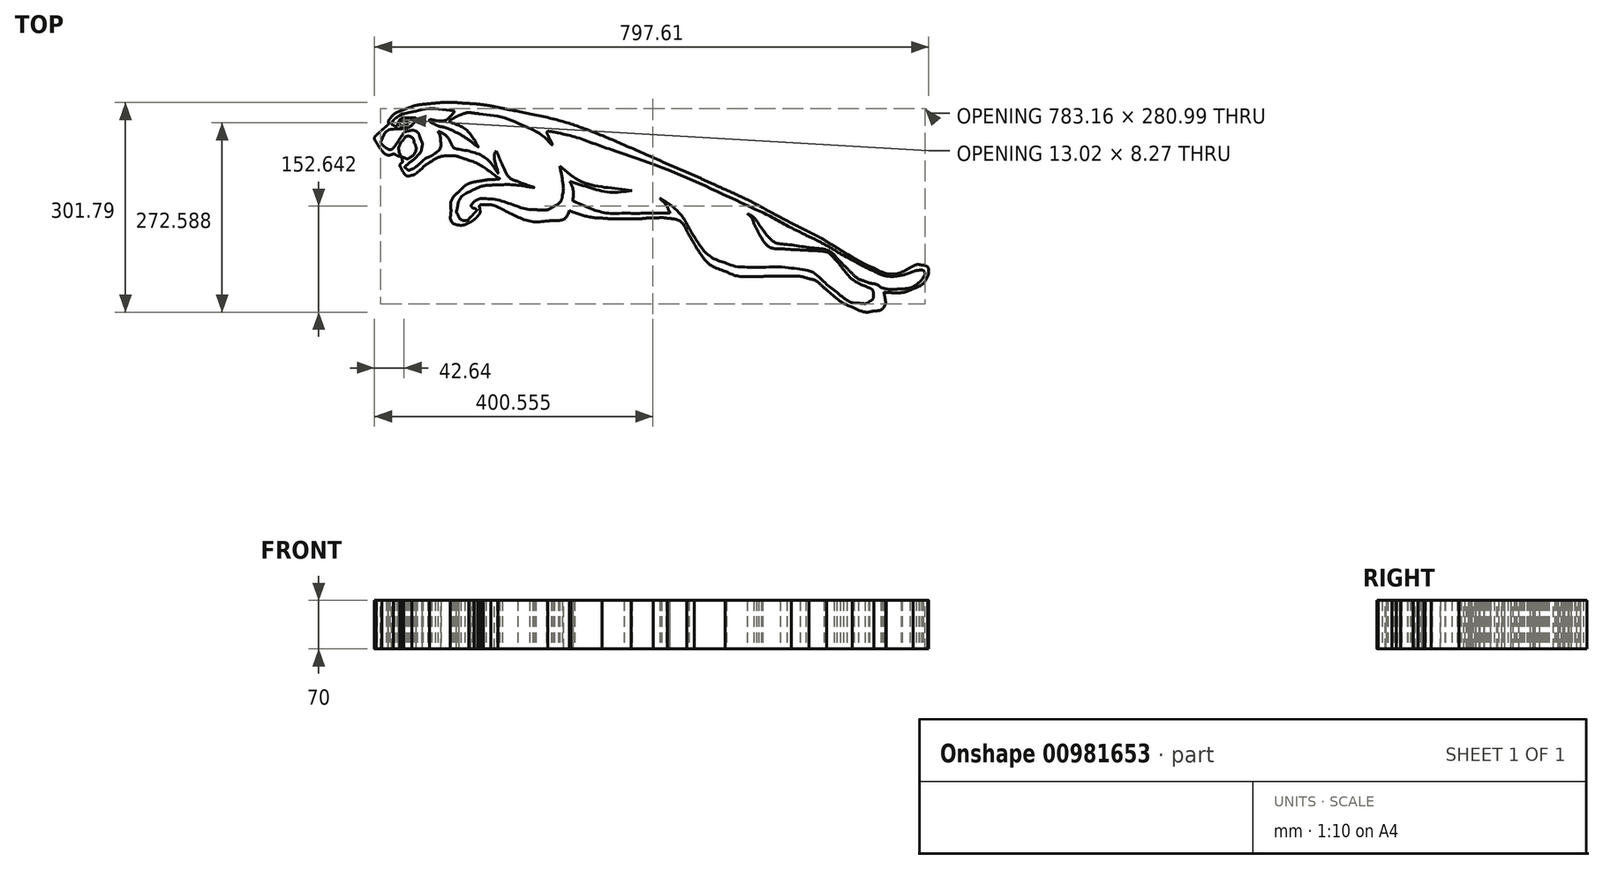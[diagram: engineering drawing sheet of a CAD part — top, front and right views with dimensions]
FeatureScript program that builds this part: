
annotation { "Feature Type Name" : "Feature", "Feature Type Description" : "" }
export const myFeature = defineFeature(function(context is Context, id is Id, definition is map)
    precondition{}
    {
        {
            var Q0;
            Q0=qCreatedBy(makeId("Top.planeOp"),FACE);
            var sketch = newSketch(context, id + "F0", { "sketchPlane" : qUnion([Q0])});
            skFitSpline(sketch, "E0", {"points": [v(-630.61, 313.95) * mm, v(-623.01, 313.31) * mm, v(-615.42, 312.58) * mm, v(-607.8, 312.06) * mm]});
            skFitSpline(sketch, "E1", {"points": [v(-607.8, 312.06) * mm, v(-564.54, 309.1) * mm, v(-521.8, 302.4) * mm, v(-479.42, 293.43) * mm]});
            skFitSpline(sketch, "E2", {"points": [v(-479.42, 293.43) * mm, v(-342.65, 264.44) * mm, v(-211.31, 218.77) * mm, v(-83.3, 163.18) * mm]});
            skFitSpline(sketch, "E3", {"points": [v(-83.3, 163.18) * mm, v(-14.33, 133.24) * mm, v(54.68, 103.37) * mm, v(123.05, 72.13) * mm]});
            skFitSpline(sketch, "E4", {"points": [v(123.05, 72.13) * mm, v(208.28, 33.18) * mm, v(290.82, -11.23) * mm, v(374.14, -54.04) * mm]});
            skFitSpline(sketch, "E5", {"points": [v(374.14, -54.04) * mm, v(421.57, -78.42) * mm, v(466.82, -106.5) * mm, v(512.74, -133.46) * mm]});
            skFitSpline(sketch, "E6", {"points": [v(512.74, -133.46) * mm, v(530.93, -144.13) * mm, v(549.79, -153.91) * mm, v(569.1, -162.39) * mm]});
            skFitSpline(sketch, "E7", {"points": [v(569.1, -162.39) * mm, v(603.9, -177.67) * mm, v(639.18, -178.12) * mm, v(673.9, -161.44) * mm]});
            skFitSpline(sketch, "E8", {"points": [v(673.9, -161.44) * mm, v(684.59, -156.3) * mm, v(695.26, -152.3) * mm, v(707.43, -154.04) * mm]});
            skFitSpline(sketch, "E9", {"points": [v(707.43, -154.04) * mm, v(718.46, -155.62) * mm, v(726.83, -162.07) * mm, v(727.59, -171.64) * mm]});
            skFitSpline(sketch, "E10", {"points": [v(727.59, -171.64) * mm, v(727.97, -176.49) * mm, v(726.73, -182.06) * mm, v(724.49, -186.41) * mm]});
            skFitSpline(sketch, "E11", {"points": [v(724.49, -186.41) * mm, v(715.53, -203.8) * mm, v(700.7, -214.79) * mm, v(682.93, -222.01) * mm]});
            skFitSpline(sketch, "E12", {"points": [v(682.93, -222.01) * mm, v(658.01, -232.15) * mm, v(631.9, -233.93) * mm, v(605.39, -232.58) * mm]});
            skFitSpline(sketch, "E13", {"points": [v(605.39, -232.58) * mm, v(603.27, -232.48) * mm, v(601.15, -232.28) * mm, v(598.96, -232.12) * mm]});
            skFitSpline(sketch, "E14", {"points": [v(598.96, -232.12) * mm, v(599.88, -237.16) * mm, v(601.07, -241.68) * mm, v(601.49, -246.27) * mm]});
            skFitSpline(sketch, "E15", {"points": [v(601.49, -246.27) * mm, v(603.35, -266.86) * mm, v(590.93, -282.73) * mm, v(570.62, -286.02) * mm]});
            skFitSpline(sketch, "E16", {"points": [v(570.62, -286.02) * mm, v(548.55, -289.6) * mm, v(527.9, -284.46) * mm, v(508.05, -275.4) * mm]});
            skFitSpline(sketch, "E17", {"points": [v(508.05, -275.4) * mm, v(480.52, -262.83) * mm, v(456.57, -244.9) * mm, v(433.9, -225.1) * mm]});
            skFitSpline(sketch, "E18", {"points": [v(433.9, -225.1) * mm, v(418.83, -211.93) * mm, v(403.61, -199.06) * mm, v(383.76, -193.24) * mm]});
            skFitSpline(sketch, "E19", {"points": [v(383.76, -193.24) * mm, v(367.16, -188.38) * mm, v(350.24, -185.59) * mm, v(333.06, -185.55) * mm]});
            skFitSpline(sketch, "E20", {"points": [v(333.06, -185.55) * mm, v(303.27, -185.5) * mm, v(273.46, -185.99) * mm, v(243.67, -186.8) * mm]});
            skFitSpline(sketch, "E21", {"points": [v(243.67, -186.8) * mm, v(208.9, -187.75) * mm, v(174.78, -184.97) * mm, v(142.17, -171.77) * mm]});
            skFitSpline(sketch, "E22", {"points": [v(142.17, -171.77) * mm, v(103.21, -156.01) * mm, v(75.08, -127.96) * mm, v(53.34, -92.86) * mm]});
            skFitSpline(sketch, "E23", {"points": [v(53.34, -92.86) * mm, v(45.71, -80.55) * mm, v(38.33, -68.06) * mm, v(31.4, -55.35) * mm]});
            skFitSpline(sketch, "E24", {"points": [v(31.4, -55.35) * mm, v(19.46, -33.42) * mm, v(0.16, -22.41) * mm, v(-23.56, -19.24) * mm]});
            skFitSpline(sketch, "E25", {"points": [v(-23.56, -19.24) * mm, v(-37, -17.45) * mm, v(-50.82, -17.88) * mm, v(-64.44, -18.27) * mm]});
            skFitSpline(sketch, "E26", {"points": [v(-64.44, -18.27) * mm, v(-85.73, -18.88) * mm, v(-107, -21.14) * mm, v(-128.29, -21.2) * mm]});
            skFitSpline(sketch, "E27", {"points": [v(-128.29, -21.2) * mm, v(-156.23, -21.27) * mm, v(-184.25, -20.92) * mm, v(-212.1, -18.86) * mm]});
            skFitSpline(sketch, "E28", {"points": [v(-212.1, -18.86) * mm, v(-243.06, -16.56) * mm, v(-273.12, -8.9) * mm, v(-302.45, 1.4) * mm]});
            skFitSpline(sketch, "E29", {"points": [v(-302.45, 1.4) * mm, v(-303.69, 1.83) * mm, v(-304.92, 2.3) * mm, v(-306.3, 2.8) * mm]});
            skFitSpline(sketch, "E30", {"points": [v(-306.3, 2.8) * mm, v(-320.32, -21.13) * mm, v(-343.94, -25.65) * mm, v(-368.29, -26.78) * mm]});
            skFitSpline(sketch, "E31", {"points": [v(-368.29, -26.78) * mm, v(-412.85, -28.83) * mm, v(-454.01, -15.8) * mm, v(-493.5, 3.77) * mm]});
            skFitSpline(sketch, "E32", {"points": [v(-493.5, 3.77) * mm, v(-512.46, 13.16) * mm, v(-532.31, 19.66) * mm, v(-553.86, 19.2) * mm]});
            skFitSpline(sketch, "E33", {"points": [v(-553.86, 19.2) * mm, v(-563.11, 19.01) * mm, v(-564.82, 16.96) * mm, v(-563.76, 7.68) * mm]});
            skFitSpline(sketch, "E34", {"points": [v(-563.76, 7.68) * mm, v(-562.94, 0.43) * mm, v(-564.55, -6.22) * mm, v(-569.2, -11.99) * mm]});
            skFitSpline(sketch, "E35", {"points": [v(-569.2, -11.99) * mm, v(-576.26, -20.7) * mm, v(-584.98, -27.6) * mm, v(-595.27, -31.64) * mm]});
            skFitSpline(sketch, "E36", {"points": [v(-595.27, -31.64) * mm, v(-615.05, -39.4) * mm, v(-644.67, -29.86) * mm, v(-646.6, 1.9) * mm]});
            skFitSpline(sketch, "E37", {"points": [v(-646.6, 1.9) * mm, v(-647.98, 24.7) * mm, v(-639.35, 43.08) * mm, v(-623.07, 58.4) * mm]});
            skFitSpline(sketch, "E38", {"points": [v(-623.07, 58.4) * mm, v(-603.35, 76.96) * mm, v(-578.99, 85.47) * mm, v(-553.01, 89.7) * mm]});
            skFitSpline(sketch, "E39", {"points": [v(-553.01, 89.7) * mm, v(-538.94, 92) * mm, v(-524.56, 92.42) * mm, v(-510.31, 93.69) * mm]});
            skFitSpline(sketch, "E40", {"points": [v(-510.31, 93.69) * mm, v(-509.4, 93.77) * mm, v(-508.48, 93.88) * mm, v(-506.71, 95.23) * mm]});
            skFitSpline(sketch, "E41", {"points": [v(-506.71, 95.23) * mm, v(-507.36, 95.43) * mm, v(-508.12, 95.48) * mm, v(-508.64, 95.86) * mm]});
            skFitSpline(sketch, "E42", {"points": [v(-508.64, 95.86) * mm, v(-539.26, 118.22) * mm, v(-571.13, 138.4) * mm, v(-606.95, 151.54) * mm]});
            skFitSpline(sketch, "E43", {"points": [v(-606.95, 151.54) * mm, v(-620.58, 156.54) * mm, v(-634.55, 160.43) * mm, v(-649.27, 160.18) * mm]});
            skFitSpline(sketch, "E44", {"points": [v(-649.27, 160.18) * mm, v(-670.86, 159.82) * mm, v(-690.52, 152.48) * mm, v(-708.53, 141.4) * mm]});
            skFitSpline(sketch, "E45", {"points": [v(-708.53, 141.4) * mm, v(-719.33, 134.76) * mm, v(-728.85, 125.93) * mm, v(-738.53, 117.6) * mm]});
            skFitSpline(sketch, "E46", {"points": [v(-738.53, 117.6) * mm, v(-744.9, 112.09) * mm, v(-751.25, 106.87) * mm, v(-759.6, 104.75) * mm]});
            skFitSpline(sketch, "E47", {"points": [v(-759.6, 104.75) * mm, v(-769.27, 102.3) * mm, v(-777.56, 104.57) * mm, v(-783.57, 112.66) * mm]});
            skFitSpline(sketch, "E48", {"points": [v(-783.57, 112.66) * mm, v(-786.4, 116.49) * mm, v(-788.45, 120.94) * mm, v(-790.55, 125.25) * mm]});
            skFitSpline(sketch, "E49", {"points": [v(-790.55, 125.25) * mm, v(-793.5, 131.3) * mm, v(-792.79, 136.76) * mm, v(-787.64, 141.58) * mm]});
            skFitSpline(sketch, "E50", {"points": [v(-787.64, 141.58) * mm, v(-786.68, 142.48) * mm, v(-786.54, 144.8) * mm, v(-786.77, 146.35) * mm]});
            skFitSpline(sketch, "E51", {"points": [v(-786.77, 146.35) * mm, v(-787.3, 150.07) * mm, v(-788.29, 153.72) * mm, v(-789.27, 158.22) * mm]});
            skFitSpline(sketch, "E52", {"points": [v(-789.27, 158.22) * mm, v(-784.78, 156.4) * mm, v(-781.3, 154.96) * mm, v(-777.79, 153.58) * mm]});
            skFitSpline(sketch, "E53", {"points": [v(-777.79, 153.58) * mm, v(-773.94, 152.07) * mm, v(-770.4, 152.52) * mm, v(-766.9, 154.88) * mm]});
            skFitSpline(sketch, "E54", {"points": [v(-766.9, 154.88) * mm, v(-753.53, 163.93) * mm, v(-747.17, 183.21) * mm, v(-752.68, 198.37) * mm]});
            skFitSpline(sketch, "E55", {"points": [v(-752.68, 198.37) * mm, v(-757.86, 212.62) * mm, v(-774.31, 216.81) * mm, v(-784.85, 205.85) * mm]});
            skFitSpline(sketch, "E56", {"points": [v(-784.85, 205.85) * mm, v(-789.78, 200.73) * mm, v(-793.7, 194.1) * mm, v(-796.28, 187.45) * mm]});
            skFitSpline(sketch, "E57", {"points": [v(-796.28, 187.45) * mm, v(-797.97, 183.09) * mm, v(-797, 177.38) * mm, v(-796.16, 172.46) * mm]});
            skFitSpline(sketch, "E58", {"points": [v(-796.16, 172.46) * mm, v(-795.45, 168.33) * mm, v(-793.19, 164.46) * mm, v(-791.44, 160.05) * mm]});
            skFitSpline(sketch, "E59", {"points": [v(-791.44, 160.05) * mm, v(-798, 159.9) * mm, v(-803.3, 161.95) * mm, v(-808.39, 164.95) * mm]});
            skFitSpline(sketch, "E60", {"points": [v(-808.39, 164.95) * mm, v(-809.63, 165.68) * mm, v(-811.44, 166.37) * mm, v(-812.7, 166.03) * mm]});
            skFitSpline(sketch, "E61", {"points": [v(-812.7, 166.03) * mm, v(-826.32, 162.38) * mm, v(-837.7, 166.75) * mm, v(-846.43, 176.85) * mm]});
            skFitSpline(sketch, "E62", {"points": [v(-846.43, 176.85) * mm, v(-852.8, 184.21) * mm, v(-858.12, 192.64) * mm, v(-862.9, 201.16) * mm]});
            skFitSpline(sketch, "E63", {"points": [v(-862.9, 201.16) * mm, v(-866.9, 208.3) * mm, v(-866, 216.02) * mm, v(-859.86, 221.84) * mm]});
            skFitSpline(sketch, "E64", {"points": [v(-859.86, 221.84) * mm, v(-850.08, 231.09) * mm, v(-839.91, 239.94) * mm, v(-829.68, 248.69) * mm]});
            skFitSpline(sketch, "E65", {"points": [v(-829.68, 248.69) * mm, v(-827.24, 250.77) * mm, v(-826.6, 252.48) * mm, v(-826.63, 255.73) * mm]});
            skFitSpline(sketch, "E66", {"points": [v(-826.63, 255.73) * mm, v(-826.65, 259.35) * mm, v(-825.52, 263.77) * mm, v(-823.26, 266.48) * mm]});
            skFitSpline(sketch, "E67", {"points": [v(-823.26, 266.48) * mm, v(-811.62, 280.44) * mm, v(-795.95, 288.55) * mm, v(-779.26, 294.82) * mm]});
            skFitSpline(sketch, "E68", {"points": [v(-779.26, 294.82) * mm, v(-753.04, 304.68) * mm, v(-725.67, 309.2) * mm, v(-697.92, 311.89) * mm]});
            skFitSpline(sketch, "E69", {"points": [v(-697.92, 311.89) * mm, v(-690.49, 312.6) * mm, v(-683.05, 313.26) * mm, v(-675.61, 313.95) * mm]});
            skFitSpline(sketch, "E70", {"points": [v(-630.61, 313.95) * mm, v(-623.01, 313.31) * mm, v(-615.42, 312.58) * mm, v(-607.8, 312.06) * mm, v(-564.54, 309.1) * mm, v(-521.8, 302.4) * mm, v(-479.42, 293.43) * mm, v(-342.65, 264.44) * mm, v(-211.31, 218.77) * mm, v(-83.3, 163.18) * mm]});
            skFitSpline(sketch, "E71", {"points": [v(-83.3, 163.18) * mm, v(-14.33, 133.24) * mm, v(54.68, 103.37) * mm, v(123.05, 72.13) * mm, v(208.28, 33.18) * mm, v(290.82, -11.23) * mm, v(374.14, -54.04) * mm]});
            skFitSpline(sketch, "E72", {"points": [v(374.14, -54.04) * mm, v(421.57, -78.42) * mm, v(466.82, -106.5) * mm, v(512.74, -133.46) * mm, v(530.93, -144.13) * mm, v(549.79, -153.91) * mm, v(569.1, -162.39) * mm]});
            skFitSpline(sketch, "E73", {"points": [v(569.1, -162.39) * mm, v(603.9, -177.67) * mm, v(639.18, -178.12) * mm, v(673.9, -161.44) * mm]});
            skFitSpline(sketch, "E74", {"points": [v(673.9, -161.44) * mm, v(684.59, -156.3) * mm, v(695.26, -152.3) * mm, v(707.43, -154.04) * mm]});
            skFitSpline(sketch, "E75", {"points": [v(707.43, -154.04) * mm, v(718.46, -155.62) * mm, v(726.83, -162.07) * mm, v(727.59, -171.64) * mm]});
            skFitSpline(sketch, "E76", {"points": [v(727.59, -171.64) * mm, v(727.97, -176.49) * mm, v(726.73, -182.06) * mm, v(724.49, -186.41) * mm]});
            skFitSpline(sketch, "E77", {"points": [v(724.49, -186.41) * mm, v(715.53, -203.8) * mm, v(700.7, -214.79) * mm, v(682.93, -222.01) * mm]});
            skFitSpline(sketch, "E78", {"points": [v(682.93, -222.01) * mm, v(658.01, -232.15) * mm, v(631.9, -233.93) * mm, v(605.39, -232.58) * mm]});
            skFitSpline(sketch, "E79", {"points": [v(605.39, -232.58) * mm, v(603.27, -232.48) * mm, v(601.15, -232.28) * mm, v(598.96, -232.12) * mm]});
            skFitSpline(sketch, "E80", {"points": [v(598.96, -232.12) * mm, v(599.88, -237.16) * mm, v(601.07, -241.68) * mm, v(601.49, -246.27) * mm]});
            skFitSpline(sketch, "E81", {"points": [v(601.49, -246.27) * mm, v(603.35, -266.86) * mm, v(590.93, -282.73) * mm, v(570.62, -286.02) * mm]});
            skFitSpline(sketch, "E82", {"points": [v(570.62, -286.02) * mm, v(548.55, -289.6) * mm, v(527.9, -284.46) * mm, v(508.05, -275.4) * mm]});
            skFitSpline(sketch, "E83", {"points": [v(508.05, -275.4) * mm, v(480.52, -262.83) * mm, v(456.57, -244.9) * mm, v(433.9, -225.1) * mm]});
            skFitSpline(sketch, "E84", {"points": [v(433.9, -225.1) * mm, v(418.83, -211.93) * mm, v(403.61, -199.06) * mm, v(383.76, -193.24) * mm]});
            skFitSpline(sketch, "E85", {"points": [v(383.76, -193.24) * mm, v(367.16, -188.38) * mm, v(350.24, -185.59) * mm, v(333.06, -185.55) * mm]});
            skFitSpline(sketch, "E86", {"points": [v(333.06, -185.55) * mm, v(303.27, -185.5) * mm, v(273.46, -185.99) * mm, v(243.67, -186.8) * mm]});
            skFitSpline(sketch, "E87", {"points": [v(243.67, -186.8) * mm, v(208.9, -187.75) * mm, v(174.78, -184.97) * mm, v(142.17, -171.77) * mm]});
            skFitSpline(sketch, "E88", {"points": [v(142.17, -171.77) * mm, v(103.21, -156.01) * mm, v(75.08, -127.96) * mm, v(53.34, -92.86) * mm]});
            skFitSpline(sketch, "E89", {"points": [v(53.34, -92.86) * mm, v(45.71, -80.55) * mm, v(38.33, -68.06) * mm, v(31.4, -55.35) * mm]});
            skFitSpline(sketch, "E90", {"points": [v(31.4, -55.35) * mm, v(19.46, -33.42) * mm, v(0.16, -22.41) * mm, v(-23.56, -19.24) * mm]});
            skFitSpline(sketch, "E91", {"points": [v(-23.56, -19.24) * mm, v(-37, -17.45) * mm, v(-50.82, -17.88) * mm, v(-64.44, -18.27) * mm]});
            skFitSpline(sketch, "E92", {"points": [v(-64.44, -18.27) * mm, v(-85.73, -18.88) * mm, v(-107, -21.14) * mm, v(-128.29, -21.2) * mm]});
            skFitSpline(sketch, "E93", {"points": [v(-128.29, -21.2) * mm, v(-156.23, -21.27) * mm, v(-184.25, -20.92) * mm, v(-212.1, -18.86) * mm]});
            skFitSpline(sketch, "E94", {"points": [v(-212.1, -18.86) * mm, v(-243.06, -16.56) * mm, v(-273.12, -8.9) * mm, v(-302.45, 1.4) * mm]});
            skFitSpline(sketch, "E95", {"points": [v(-302.45, 1.4) * mm, v(-303.69, 1.83) * mm, v(-304.92, 2.3) * mm, v(-306.3, 2.8) * mm]});
            skFitSpline(sketch, "E96", {"points": [v(-306.3, 2.8) * mm, v(-320.32, -21.13) * mm, v(-343.94, -25.65) * mm, v(-368.29, -26.78) * mm]});
            skFitSpline(sketch, "E97", {"points": [v(-368.29, -26.78) * mm, v(-412.85, -28.83) * mm, v(-454.01, -15.8) * mm, v(-493.5, 3.77) * mm]});
            skFitSpline(sketch, "E98", {"points": [v(-493.5, 3.77) * mm, v(-512.46, 13.16) * mm, v(-532.31, 19.66) * mm, v(-553.86, 19.2) * mm, v(-563.11, 19.01) * mm, v(-564.82, 16.96) * mm, v(-563.76, 7.68) * mm]});
            skFitSpline(sketch, "E99", {"points": [v(-563.76, 7.68) * mm, v(-562.94, 0.43) * mm, v(-564.55, -6.22) * mm, v(-569.2, -11.99) * mm]});
            skFitSpline(sketch, "E100", {"points": [v(-569.2, -11.99) * mm, v(-572.73, -16.35) * mm, v(-576.67, -20.25) * mm, v(-581.02, -23.57) * mm]});
            skFitSpline(sketch, "E101", {"points": [v(-581.02, -23.57) * mm, v(-585.37, -26.89) * mm, v(-590.12, -29.62) * mm, v(-595.27, -31.64) * mm]});
            skFitSpline(sketch, "E102", {"points": [v(-595.27, -31.64) * mm, v(-615.05, -39.4) * mm, v(-644.67, -29.86) * mm, v(-646.6, 1.9) * mm]});
            skFitSpline(sketch, "E103", {"points": [v(-646.6, 1.9) * mm, v(-647.98, 24.7) * mm, v(-639.35, 43.08) * mm, v(-623.07, 58.4) * mm]});
            skFitSpline(sketch, "E104", {"points": [v(-623.07, 58.4) * mm, v(-603.35, 76.96) * mm, v(-578.99, 85.47) * mm, v(-553.01, 89.7) * mm, v(-538.94, 92) * mm, v(-524.56, 92.42) * mm, v(-510.31, 93.69) * mm]});
            skFitSpline(sketch, "E105", {"points": [v(-510.31, 93.69) * mm, v(-509.4, 93.77) * mm, v(-508.48, 93.88) * mm, v(-506.71, 95.23) * mm]});
            skFitSpline(sketch, "E106", {"points": [v(-506.71, 95.23) * mm, v(-507.36, 95.43) * mm, v(-508.12, 95.48) * mm, v(-508.64, 95.86) * mm]});
            skFitSpline(sketch, "E107", {"points": [v(-508.64, 95.86) * mm, v(-539.26, 118.22) * mm, v(-571.13, 138.4) * mm, v(-606.95, 151.54) * mm]});
            skFitSpline(sketch, "E108", {"points": [v(-606.95, 151.54) * mm, v(-620.58, 156.54) * mm, v(-634.55, 160.43) * mm, v(-649.27, 160.18) * mm]});
            skFitSpline(sketch, "E109", {"points": [v(-649.27, 160.18) * mm, v(-670.86, 159.82) * mm, v(-690.52, 152.48) * mm, v(-708.53, 141.4) * mm]});
            skFitSpline(sketch, "E110", {"points": [v(-708.53, 141.4) * mm, v(-719.33, 134.76) * mm, v(-728.85, 125.93) * mm, v(-738.53, 117.6) * mm]});
            skFitSpline(sketch, "E111", {"points": [v(-738.53, 117.6) * mm, v(-744.9, 112.09) * mm, v(-751.25, 106.87) * mm, v(-759.6, 104.75) * mm]});
            skFitSpline(sketch, "E112", {"points": [v(-759.6, 104.75) * mm, v(-769.27, 102.3) * mm, v(-777.56, 104.57) * mm, v(-783.57, 112.66) * mm]});
            skFitSpline(sketch, "E113", {"points": [v(-783.57, 112.66) * mm, v(-786.4, 116.49) * mm, v(-788.45, 120.94) * mm, v(-790.55, 125.25) * mm]});
            skFitSpline(sketch, "E114", {"points": [v(-790.55, 125.25) * mm, v(-793.5, 131.3) * mm, v(-792.79, 136.76) * mm, v(-787.64, 141.58) * mm]});
            skFitSpline(sketch, "E115", {"points": [v(-787.64, 141.58) * mm, v(-786.68, 142.48) * mm, v(-786.54, 144.8) * mm, v(-786.77, 146.35) * mm]});
            skFitSpline(sketch, "E116", {"points": [v(-786.77, 146.35) * mm, v(-787.3, 150.07) * mm, v(-788.29, 153.72) * mm, v(-789.27, 158.22) * mm]});
            skFitSpline(sketch, "E117", {"points": [v(-789.27, 158.22) * mm, v(-784.78, 156.4) * mm, v(-781.3, 154.96) * mm, v(-777.79, 153.58) * mm]});
            skFitSpline(sketch, "E118", {"points": [v(-777.79, 153.58) * mm, v(-773.94, 152.07) * mm, v(-770.4, 152.52) * mm, v(-766.9, 154.88) * mm]});
            skFitSpline(sketch, "E119", {"points": [v(-766.9, 154.88) * mm, v(-753.53, 163.93) * mm, v(-747.17, 183.21) * mm, v(-752.68, 198.37) * mm]});
            skFitSpline(sketch, "E120", {"points": [v(-752.68, 198.37) * mm, v(-757.86, 212.62) * mm, v(-774.31, 216.81) * mm, v(-784.85, 205.85) * mm]});
            skFitSpline(sketch, "E121", {"points": [v(-784.85, 205.85) * mm, v(-789.78, 200.73) * mm, v(-793.7, 194.1) * mm, v(-796.28, 187.45) * mm]});
            skFitSpline(sketch, "E122", {"points": [v(-796.28, 187.45) * mm, v(-797.97, 183.09) * mm, v(-797, 177.38) * mm, v(-796.16, 172.46) * mm]});
            skFitSpline(sketch, "E123", {"points": [v(-796.16, 172.46) * mm, v(-795.45, 168.33) * mm, v(-793.19, 164.46) * mm, v(-791.44, 160.05) * mm]});
            skFitSpline(sketch, "E124", {"points": [v(-791.44, 160.05) * mm, v(-798, 159.9) * mm, v(-803.3, 161.95) * mm, v(-808.39, 164.95) * mm]});
            skFitSpline(sketch, "E125", {"points": [v(-808.39, 164.95) * mm, v(-809.63, 165.68) * mm, v(-811.44, 166.37) * mm, v(-812.7, 166.03) * mm]});
            skFitSpline(sketch, "E126", {"points": [v(-812.7, 166.03) * mm, v(-826.32, 162.38) * mm, v(-837.7, 166.75) * mm, v(-846.43, 176.85) * mm]});
            skFitSpline(sketch, "E127", {"points": [v(-846.43, 176.85) * mm, v(-852.8, 184.21) * mm, v(-858.12, 192.64) * mm, v(-862.9, 201.16) * mm]});
            skFitSpline(sketch, "E128", {"points": [v(-862.9, 201.16) * mm, v(-866.9, 208.3) * mm, v(-866, 216.02) * mm, v(-859.86, 221.84) * mm]});
            skFitSpline(sketch, "E129", {"points": [v(-859.86, 221.84) * mm, v(-850.08, 231.09) * mm, v(-839.91, 239.94) * mm, v(-829.68, 248.69) * mm, v(-827.24, 250.77) * mm, v(-826.6, 252.48) * mm, v(-826.63, 255.73) * mm]});
            skFitSpline(sketch, "E130", {"points": [v(-826.63, 255.73) * mm, v(-826.65, 259.35) * mm, v(-825.52, 263.77) * mm, v(-823.27, 266.48) * mm]});
            skFitSpline(sketch, "E131", {"points": [v(-823.27, 266.48) * mm, v(-811.62, 280.44) * mm, v(-795.95, 288.55) * mm, v(-779.27, 294.82) * mm, v(-753.04, 304.68) * mm, v(-725.67, 309.2) * mm, v(-697.92, 311.89) * mm, v(-690.49, 312.6) * mm, v(-683.05, 313.26) * mm, v(-675.61, 313.95) * mm]});
            skFitSpline(sketch, "E132", {"points": [v(-675.61, 313.95) * mm, v(-660.61, 313.95) * mm, v(-645.61, 313.95) * mm, v(-630.61, 313.95) * mm]});
            skFitSpline(sketch, "E133", {"points": [v(205.03, -5.67) * mm, v(219.16, -13.12) * mm, v(230.59, -23.28) * mm, v(239.13, -36.66) * mm]});
            skFitSpline(sketch, "E134", {"points": [v(239.13, -36.66) * mm, v(242.53, -41.98) * mm, v(246.44, -47) * mm, v(250.27, -52.02) * mm]});
            skFitSpline(sketch, "E135", {"points": [v(250.27, -52.02) * mm, v(267.87, -75.08) * mm, v(290.2, -90.44) * mm, v(319.5, -94.4) * mm]});
            skFitSpline(sketch, "E136", {"points": [v(319.5, -94.4) * mm, v(348.36, -98.3) * mm, v(377.19, -102.57) * mm, v(406.1, -106.03) * mm, v(428.63, -108.74) * mm, v(448.05, -116.97) * mm, v(463.7, -133.78) * mm]});
            skFitSpline(sketch, "E137", {"points": [v(463.7, -133.78) * mm, v(474.02, -144.87) * mm, v(484.74, -155.6) * mm, v(495.44, -166.35) * mm]});
            skFitSpline(sketch, "E138", {"points": [v(495.44, -166.35) * mm, v(509.75, -180.72) * mm, v(525.18, -193.38) * mm, v(544.57, -200.7) * mm]});
            skFitSpline(sketch, "E139", {"points": [v(544.57, -200.7) * mm, v(559.75, -206.41) * mm, v(576.2, -208.93) * mm, v(589.95, -218.37) * mm]});
            skFitSpline(sketch, "E140", {"points": [v(589.95, -218.37) * mm, v(591.38, -219.35) * mm, v(593.4, -219.55) * mm, v(595.19, -219.93) * mm]});
            skFitSpline(sketch, "E141", {"points": [v(595.19, -219.93) * mm, v(612.77, -223.66) * mm, v(630.55, -223.92) * mm, v(648.4, -222.68) * mm]});
            skFitSpline(sketch, "E142", {"points": [v(648.4, -222.68) * mm, v(668, -221.32) * mm, v(686.02, -215.35) * mm, v(701.25, -202.76) * mm]});
            skFitSpline(sketch, "E143", {"points": [v(701.25, -202.76) * mm, v(705.96, -198.87) * mm, v(710.23, -193.6) * mm, v(712.73, -188.08) * mm]});
            skFitSpline(sketch, "E144", {"points": [v(712.73, -188.08) * mm, v(717.26, -178.07) * mm, v(710.3, -168.73) * mm, v(699.32, -168.84) * mm]});
            skFitSpline(sketch, "E145", {"points": [v(699.32, -168.84) * mm, v(696.84, -168.86) * mm, v(694.24, -168.99) * mm, v(691.93, -169.77) * mm]});
            skFitSpline(sketch, "E146", {"points": [v(691.93, -169.77) * mm, v(683.27, -172.68) * mm, v(674.75, -176) * mm, v(666.1, -178.92) * mm]});
            skFitSpline(sketch, "E147", {"points": [v(666.1, -178.92) * mm, v(661.24, -180.56) * mm, v(656.3, -182.31) * mm, v(651.26, -182.98) * mm]});
            skFitSpline(sketch, "E148", {"points": [v(651.26, -182.98) * mm, v(623, -186.7) * mm, v(595.41, -182.77) * mm, v(569.72, -171.12) * mm]});
            skFitSpline(sketch, "E149", {"points": [v(569.72, -171.12) * mm, v(543.25, -159.1) * mm, v(517.63, -145.14) * mm, v(492.05, -131.25) * mm]});
            skFitSpline(sketch, "E150", {"points": [v(492.05, -131.25) * mm, v(469.83, -119.2) * mm, v(448.48, -105.52) * mm, v(426.21, -93.53) * mm]});
            skFitSpline(sketch, "E151", {"points": [v(426.21, -93.53) * mm, v(403.96, -81.55) * mm, v(381, -70.88) * mm, v(358.44, -59.44) * mm]});
            skFitSpline(sketch, "E152", {"points": [v(358.44, -59.44) * mm, v(313.78, -36.77) * mm, v(269.82, -12.63) * mm, v(224.46, 8.53) * mm]});
            skFitSpline(sketch, "E153", {"points": [v(224.46, 8.53) * mm, v(90.23, 71.14) * mm, v(-45.9, 129.3) * mm, v(-185.76, 178.4) * mm]});
            skFitSpline(sketch, "E154", {"points": [v(-185.76, 178.4) * mm, v(-236, 196.03) * mm, v(-286.2, 213.74) * mm, v(-337.98, 226.42) * mm]});
            skFitSpline(sketch, "E155", {"points": [v(-337.98, 226.42) * mm, v(-347, 228.63) * mm, v(-356.24, 230.07) * mm, v(-365.44, 231.44) * mm, v(-367.4, 231.74) * mm, v(-369.63, 230.22) * mm, v(-371.73, 229.54) * mm]});
            skFitSpline(sketch, "E156", {"points": [v(-371.73, 229.54) * mm, v(-371.1, 227.76) * mm, v(-370.6, 225.9) * mm, v(-369.8, 224.2) * mm]});
            skFitSpline(sketch, "E157", {"points": [v(-369.8, 224.2) * mm, v(-364.86, 213.77) * mm, v(-359.86, 203.36) * mm, v(-354.88, 192.94) * mm]});
            skFitSpline(sketch, "E158", {"points": [v(-354.88, 192.94) * mm, v(-355.38, 192.66) * mm, v(-355.88, 192.37) * mm, v(-356.38, 192.09) * mm]});
            skFitSpline(sketch, "E159", {"points": [v(-356.38, 192.09) * mm, v(-356.98, 192.55) * mm, v(-357.65, 192.95) * mm, v(-358.18, 193.48) * mm]});
            skFitSpline(sketch, "E160", {"points": [v(-358.18, 193.48) * mm, v(-381.84, 217.37) * mm, v(-409.85, 234.75) * mm, v(-440.4, 248.3) * mm, v(-480.6, 266.13) * mm, v(-522.8, 276.49) * mm, v(-566.3, 281.85) * mm]});
            skFitSpline(sketch, "E161", {"points": [v(-566.3, 281.85) * mm, v(-583.8, 284.01) * mm, v(-601.4, 284.77) * mm, v(-618.23, 278.84) * mm]});
            skFitSpline(sketch, "E162", {"points": [v(-618.23, 278.84) * mm, v(-628.32, 275.28) * mm, v(-637.75, 269.81) * mm, v(-647.31, 264.89) * mm]});
            skFitSpline(sketch, "E163", {"points": [v(-647.31, 264.89) * mm, v(-648.9, 264.07) * mm, v(-650.41, 261.65) * mm, v(-650.48, 259.9) * mm, v(-650.52, 258.8) * mm, v(-647.94, 257.4) * mm, v(-646.34, 256.47) * mm]});
            skFitSpline(sketch, "E164", {"points": [v(-646.34, 256.47) * mm, v(-644.78, 255.57) * mm, v(-642.94, 255.15) * mm, v(-641.26, 254.42) * mm]});
            skFitSpline(sketch, "E165", {"points": [v(-641.26, 254.42) * mm, v(-609.02, 240.28) * mm, v(-586.24, 215.93) * mm, v(-568.06, 186.6) * mm]});
            skFitSpline(sketch, "E166", {"points": [v(-568.06, 186.6) * mm, v(-567.98, 186.48) * mm, v(-568.27, 186.12) * mm, v(-568.48, 185.7) * mm]});
            skFitSpline(sketch, "E167", {"points": [v(-568.48, 185.7) * mm, v(-570.35, 187.13) * mm, v(-572.2, 188.53) * mm, v(-574.04, 189.95) * mm]});
            skFitSpline(sketch, "E168", {"points": [v(-574.04, 189.95) * mm, v(-592.36, 204.16) * mm, v(-611.47, 217.2) * mm, v(-632.05, 227.94) * mm]});
            skFitSpline(sketch, "E169", {"points": [v(-632.05, 227.94) * mm, v(-645.8, 235.12) * mm, v(-660.01, 240.87) * mm, v(-675.27, 244.44) * mm]});
            skFitSpline(sketch, "E170", {"points": [v(-675.27, 244.44) * mm, v(-684.48, 246.6) * mm, v(-693.22, 251.16) * mm, v(-701.81, 255.38) * mm]});
            skFitSpline(sketch, "E171", {"points": [v(-701.81, 255.38) * mm, v(-705.38, 257.14) * mm, v(-708.53, 260.53) * mm, v(-708.42, 265.67) * mm]});
            skFitSpline(sketch, "E172", {"points": [v(-708.42, 265.67) * mm, v(-705.72, 265.18) * mm, v(-703.46, 264.7) * mm, v(-701.17, 264.36) * mm, v(-677.4, 260.88) * mm, v(-656.61, 266.8) * mm, v(-639.55, 284.15) * mm, v(-638.31, 285.4) * mm, v(-637.93, 287.5) * mm, v(-637.14, 289.22) * mm]});
            skFitSpline(sketch, "E173", {"points": [v(-637.14, 289.22) * mm, v(-638.75, 289.88) * mm, v(-640.32, 290.96) * mm, v(-641.98, 291.14) * mm, v(-679.25, 295.26) * mm, v(-716.43, 295.75) * mm, v(-753.35, 287.94) * mm, v(-770.64, 284.29) * mm, v(-787.93, 280.43) * mm, v(-803.14, 270.88) * mm]});
            skFitSpline(sketch, "E174", {"points": [v(-803.14, 270.88) * mm, v(-807.55, 268.1) * mm, v(-811.47, 264.25) * mm, v(-814.85, 260.24) * mm]});
            skFitSpline(sketch, "E175", {"points": [v(-814.85, 260.24) * mm, v(-818.24, 256.23) * mm, v(-816.63, 250.74) * mm, v(-812.2, 248.3) * mm, v(-806.91, 245.4) * mm, v(-802.58, 246.64) * mm, v(-800.28, 251.7) * mm]});
            skFitSpline(sketch, "E176", {"points": [v(-800.28, 251.7) * mm, v(-795.12, 263) * mm, v(-786.66, 269.5) * mm, v(-773.94, 269.87) * mm, v(-771.28, 269.95) * mm, v(-768.62, 270.34) * mm, v(-765.96, 270.24) * mm, v(-759.1, 270) * mm, v(-752.1, 270.34) * mm, v(-745.32, 266.64) * mm]});
            skFitSpline(sketch, "E177", {"points": [v(-745.32, 266.64) * mm, v(-756.62, 252.41) * mm, v(-769.7, 241.9) * mm, v(-787.84, 239.36) * mm]});
            skFitSpline(sketch, "E178", {"points": [v(-787.84, 239.36) * mm, v(-793.27, 238.6) * mm, v(-798.82, 238.7) * mm, v(-804.27, 238.05) * mm, v(-823.25, 235.8) * mm, v(-837.04, 225.9) * mm, v(-845.8, 209.04) * mm, v(-848.62, 203.64) * mm, v(-848.93, 197.8) * mm, v(-844.76, 193.08) * mm]});
            skFitSpline(sketch, "E179", {"points": [v(-844.76, 193.08) * mm, v(-841.3, 189.17) * mm, v(-837.2, 185.45) * mm, v(-832.66, 182.96) * mm]});
            skFitSpline(sketch, "E180", {"points": [v(-832.66, 182.96) * mm, v(-824.16, 178.31) * mm, v(-816.17, 180.13) * mm, v(-809.67, 187.35) * mm]});
            skFitSpline(sketch, "E181", {"points": [v(-809.67, 187.35) * mm, v(-807.23, 190.05) * mm, v(-805.2, 193.14) * mm, v(-803.19, 196.19) * mm]});
            skFitSpline(sketch, "E182", {"points": [v(-803.19, 196.19) * mm, v(-797.58, 204.65) * mm, v(-792.25, 213.3) * mm, v(-786.49, 221.65) * mm]});
            skFitSpline(sketch, "E183", {"points": [v(-786.49, 221.65) * mm, v(-782.53, 227.39) * mm, v(-776.73, 230.72) * mm, v(-769.84, 231.73) * mm]});
            skFitSpline(sketch, "E184", {"points": [v(-769.84, 231.73) * mm, v(-755.23, 233.88) * mm, v(-741.37, 226.63) * mm, v(-735.67, 212.97) * mm, v(-730.7, 201.06) * mm, v(-729.4, 191.4) * mm, v(-731.13, 182.91) * mm]});
            skFitSpline(sketch, "E185", {"points": [v(-731.13, 182.91) * mm, v(-732.87, 174.42) * mm, v(-737.63, 167.08) * mm, v(-744.8, 159.78) * mm]});
            skFitSpline(sketch, "E186", {"points": [v(-744.8, 159.78) * mm, v(-754.1, 150.32) * mm, v(-764.66, 142.09) * mm, v(-774.9, 133.58) * mm]});
            skFitSpline(sketch, "E187", {"points": [v(-774.9, 133.58) * mm, v(-779.63, 129.63) * mm, v(-780, 127.33) * mm, v(-775.28, 123.38) * mm]});
            skFitSpline(sketch, "E188", {"points": [v(-775.28, 123.38) * mm, v(-771.88, 120.55) * mm, v(-767.91, 118.89) * mm, v(-763.7, 120.53) * mm]});
            skFitSpline(sketch, "E189", {"points": [v(-763.7, 120.53) * mm, v(-758.82, 122.44) * mm, v(-753.74, 124.51) * mm, v(-749.64, 127.67) * mm]});
            skFitSpline(sketch, "E190", {"points": [v(-749.64, 127.67) * mm, v(-742.14, 133.46) * mm, v(-735.2, 139.97) * mm, v(-728.24, 146.42) * mm]});
            skFitSpline(sketch, "E191", {"points": [v(-728.24, 146.42) * mm, v(-724.07, 150.3) * mm, v(-719.7, 153.34) * mm, v(-714.34, 155.66) * mm]});
            skFitSpline(sketch, "E192", {"points": [v(-714.34, 155.66) * mm, v(-706.62, 158.99) * mm, v(-699.04, 163.16) * mm, v(-692.37, 168.25) * mm]});
            skFitSpline(sketch, "E193", {"points": [v(-692.37, 168.25) * mm, v(-681.1, 176.86) * mm, v(-675.81, 188.76) * mm, v(-676.62, 203.18) * mm, v(-677.19, 213.22) * mm, v(-679.77, 222.65) * mm, v(-684.69, 231.76) * mm]});
            skFitSpline(sketch, "E194", {"points": [v(-684.69, 231.76) * mm, v(-680.15, 230.19) * mm, v(-675.78, 228.57) * mm, v(-671.96, 226.1) * mm, v(-660.61, 218.72) * mm, v(-652.87, 208.1) * mm, v(-646.79, 196.27) * mm]});
            skFitSpline(sketch, "E195", {"points": [v(-646.79, 196.27) * mm, v(-642.15, 187.24) * mm, v(-635.43, 181.77) * mm, v(-625.2, 179.62) * mm]});
            skFitSpline(sketch, "E196", {"points": [v(-625.2, 179.62) * mm, v(-579.72, 170.03) * mm, v(-540.91, 149.17) * mm, v(-512.51, 111.27) * mm]});
            skFitSpline(sketch, "E197", {"points": [v(-512.51, 111.27) * mm, v(-512.12, 110.75) * mm, v(-511.54, 110.36) * mm, v(-510.55, 109.45) * mm]});
            skFitSpline(sketch, "E198", {"points": [v(-510.55, 109.45) * mm, v(-520.18, 143.25) * mm, v(-522.03, 165.88) * mm, v(-516.32, 174.5) * mm]});
            skFitSpline(sketch, "E199", {"points": [v(-516.32, 174.5) * mm, v(-510.62, 161.3) * mm, v(-505, 147.8) * mm, v(-498.98, 134.48) * mm]});
            skFitSpline(sketch, "E200", {"points": [v(-498.98, 134.48) * mm, v(-489.62, 113.74) * mm, v(-476.6, 96.14) * mm, v(-454.93, 86.86) * mm]});
            skFitSpline(sketch, "E201", {"points": [v(-454.93, 86.86) * mm, v(-443.8, 82.1) * mm, v(-432.33, 78.07) * mm, v(-420.94, 73.91) * mm]});
            skFitSpline(sketch, "E202", {"points": [v(-420.94, 73.91) * mm, v(-416.29, 72.21) * mm, v(-411.44, 71.05) * mm, v(-406.69, 69.64) * mm]});
            skFitSpline(sketch, "E203", {"points": [v(-406.69, 69.64) * mm, v(-408.36, 69) * mm, v(-409.84, 69.08) * mm, v(-411.3, 69.32) * mm]});
            skFitSpline(sketch, "E204", {"points": [v(-411.3, 69.32) * mm, v(-445.56, 74.95) * mm, v(-480.02, 77.77) * mm, v(-514.77, 76.62) * mm]});
            skFitSpline(sketch, "E205", {"points": [v(-514.77, 76.62) * mm, v(-539.3, 75.8) * mm, v(-563.1, 71.8) * mm, v(-585.44, 61.1) * mm]});
            skFitSpline(sketch, "E206", {"points": [v(-585.44, 61.1) * mm, v(-606.2, 51.15) * mm, v(-621.63, 36.42) * mm, v(-628.07, 13.61) * mm, v(-630.26, 5.84) * mm, v(-630.67, -1.78) * mm, v(-626.76, -9.2) * mm]});
            skFitSpline(sketch, "E207", {"points": [v(-626.76, -9.2) * mm, v(-620.04, -21.97) * mm, v(-603.33, -26.04) * mm, v(-592.29, -17) * mm]});
            skFitSpline(sketch, "E208", {"points": [v(-592.29, -17) * mm, v(-586.93, -12.62) * mm, v(-582.43, -7.16) * mm, v(-577.78, -1.97) * mm]});
            skFitSpline(sketch, "E209", {"points": [v(-577.78, -1.97) * mm, v(-573.4, 2.92) * mm, v(-574.36, 7.02) * mm, v(-580.62, 9.53) * mm]});
            skFitSpline(sketch, "E210", {"points": [v(-580.62, 9.53) * mm, v(-586.65, 11.94) * mm, v(-588.8, 18.4) * mm, v(-584.94, 23.57) * mm]});
            skFitSpline(sketch, "E211", {"points": [v(-584.94, 23.57) * mm, v(-582.12, 27.36) * mm, v(-577.84, 30.6) * mm, v(-573.53, 32.65) * mm]});
            skFitSpline(sketch, "E212", {"points": [v(-573.53, 32.65) * mm, v(-565.13, 36.6) * mm, v(-555.94, 37.5) * mm, v(-546.67, 36.96) * mm]});
            skFitSpline(sketch, "E213", {"points": [v(-546.67, 36.96) * mm, v(-519.99, 35.41) * mm, v(-494.46, 28.56) * mm, v(-469.4, 19.81) * mm, v(-447.77, 12.25) * mm, v(-425.73, 6.7) * mm, v(-402.78, 5.48) * mm]});
            skFitSpline(sketch, "E214", {"points": [v(-402.78, 5.48) * mm, v(-384.25, 4.5) * mm, v(-366.14, 6.38) * mm, v(-349.62, 15.86) * mm]});
            skFitSpline(sketch, "E215", {"points": [v(-349.62, 15.86) * mm, v(-337.15, 23.03) * mm, v(-328.89, 33.33) * mm, v(-326.14, 47.76) * mm]});
            skFitSpline(sketch, "E216", {"points": [v(-326.14, 47.76) * mm, v(-323.43, 62.03) * mm, v(-324.04, 76.32) * mm, v(-326.2, 90.51) * mm, v(-328.31, 104.45) * mm, v(-331.23, 118.27) * mm, v(-333.75, 131.9) * mm]});
            skFitSpline(sketch, "E217", {"points": [v(-333.75, 131.9) * mm, v(-272.36, 86.56) * mm, v(-200.85, 69.54) * mm, v(-126.4, 60.84) * mm]});
            skFitSpline(sketch, "E218", {"points": [v(-126.4, 60.84) * mm, v(-187.48, 55.68) * mm, v(-246.06, 68.65) * mm, v(-304.63, 86.6) * mm]});
            skFitSpline(sketch, "E219", {"points": [v(-304.63, 86.6) * mm, v(-297.01, 69.45) * mm, v(-294.72, 52.24) * mm, v(-295.79, 34.56) * mm]});
            skFitSpline(sketch, "E220", {"points": [v(-295.79, 34.56) * mm, v(-296.02, 30.78) * mm, v(-293.77, 30.14) * mm, v(-291.36, 29.07) * mm]});
            skFitSpline(sketch, "E221", {"points": [v(-291.36, 29.07) * mm, v(-246, 8.98) * mm, v(-198.83, -3.97) * mm, v(-148.99, -4.55) * mm]});
            skFitSpline(sketch, "E222", {"points": [v(-148.99, -4.55) * mm, v(-106.52, -5.04) * mm, v(-64.04, -4.2) * mm, v(-21.57, -4.03) * mm]});
            skFitSpline(sketch, "E223", {"points": [v(-21.57, -4.03) * mm, v(-18.12, -4.01) * mm, v(-17.17, -2.25) * mm, v(-18.37, 0.3) * mm]});
            skFitSpline(sketch, "E224", {"points": [v(-18.37, 0.3) * mm, v(-21.3, 6.56) * mm, v(-24, 13.1) * mm, v(-28.04, 18.62) * mm]});
            skFitSpline(sketch, "E225", {"points": [v(-28.04, 18.62) * mm, v(-32.98, 25.38) * mm, v(-39.2, 31.2) * mm, v(-45.49, 38.13) * mm]});
            skFitSpline(sketch, "E226", {"points": [v(-45.49, 38.13) * mm, v(-43.6, 37.24) * mm, v(-42.38, 36.8) * mm, v(-41.31, 36.14) * mm]});
            skFitSpline(sketch, "E227", {"points": [v(-41.31, 36.14) * mm, v(-35.82, 32.68) * mm, v(-30.05, 29.58) * mm, v(-24.95, 25.61) * mm]});
            skFitSpline(sketch, "E228", {"points": [v(-24.95, 25.61) * mm, v(0.84, 5.52) * mm, v(21.88, -18.74) * mm, v(38.12, -47.16) * mm]});
            skFitSpline(sketch, "E229", {"points": [v(38.12, -47.16) * mm, v(43.32, -56.26) * mm, v(48.52, -65.4) * mm, v(54.38, -74.08) * mm]});
            skFitSpline(sketch, "E230", {"points": [v(54.38, -74.08) * mm, v(77.34, -108.06) * mm, v(106.86, -134.1) * mm, v(145.8, -148.51) * mm]});
            skFitSpline(sketch, "E231", {"points": [v(145.8, -148.51) * mm, v(166.98, -156.35) * mm, v(188.93, -159.6) * mm, v(211.39, -159.98) * mm, v(251.84, -160.68) * mm, v(292.34, -158.65) * mm, v(332.73, -162.97) * mm]});
            skFitSpline(sketch, "E232", {"points": [v(332.73, -162.97) * mm, v(366.84, -166.61) * mm, v(397.92, -176.73) * mm, v(424.13, -199.97) * mm, v(440.32, -214.34) * mm, v(457.18, -227.98) * mm, v(474.22, -241.33) * mm]});
            skFitSpline(sketch, "E233", {"points": [v(474.22, -241.33) * mm, v(489.19, -253.05) * mm, v(505.67, -261.97) * mm, v(525.17, -263.7) * mm]});
            skFitSpline(sketch, "E234", {"points": [v(525.17, -263.7) * mm, v(536.6, -264.7) * mm, v(547.88, -264.86) * mm, v(558.03, -258.34) * mm]});
            skFitSpline(sketch, "E235", {"points": [v(558.03, -258.34) * mm, v(565.96, -253.24) * mm, v(569.22, -245.62) * mm, v(568.29, -236.5) * mm]});
            skFitSpline(sketch, "E236", {"points": [v(568.29, -236.5) * mm, v(567.4, -227.84) * mm, v(562.35, -222.18) * mm, v(554.27, -218.66) * mm]});
            skFitSpline(sketch, "E237", {"points": [v(554.27, -218.66) * mm, v(526.57, -206.58) * mm, v(502.2, -189.88) * mm, v(482.77, -166.4) * mm]});
            skFitSpline(sketch, "E238", {"points": [v(482.77, -166.4) * mm, v(474.08, -155.88) * mm, v(465.81, -144.85) * mm, v(456.04, -135.41) * mm]});
            skFitSpline(sketch, "E239", {"points": [v(456.04, -135.41) * mm, v(438.01, -118) * mm, v(414.91, -113.33) * mm, v(390.75, -112.08) * mm]});
            skFitSpline(sketch, "E240", {"points": [v(390.75, -112.08) * mm, v(360.83, -110.54) * mm, v(330.9, -109.06) * mm, v(301.01, -106.89) * mm]});
            skFitSpline(sketch, "E241", {"points": [v(301.01, -106.89) * mm, v(277.24, -105.16) * mm, v(258.63, -93.66) * mm, v(245.65, -73.77) * mm]});
            skFitSpline(sketch, "E242", {"points": [v(245.65, -73.77) * mm, v(240.5, -65.87) * mm, v(236.53, -57.16) * mm, v(232.35, -48.67) * mm]});
            skFitSpline(sketch, "E243", {"points": [v(232.35, -48.67) * mm, v(224.8, -33.33) * mm, v(218.45, -17.27) * mm, v(205.03, -5.67) * mm]});
            skFitSpline(sketch, "E244", {"points": [v(-794.98, 247.88) * mm, v(-781.12, 247.6) * mm, v(-771.76, 251.81) * mm, v(-768.94, 259.43) * mm]});
            skFitSpline(sketch, "E245", {"points": [v(-768.94, 259.43) * mm, v(-782.46, 263.83) * mm, v(-792.41, 259.54) * mm, v(-794.98, 247.88) * mm]});
            skFitSpline(sketch, "E246", {"points": [v(205.03, -5.67) * mm, v(218.45, -17.27) * mm, v(224.8, -33.33) * mm, v(232.35, -48.67) * mm]});
            skFitSpline(sketch, "E247", {"points": [v(232.35, -48.67) * mm, v(236.53, -57.16) * mm, v(240.5, -65.87) * mm, v(245.65, -73.77) * mm]});
            skFitSpline(sketch, "E248", {"points": [v(245.65, -73.77) * mm, v(258.63, -93.66) * mm, v(277.24, -105.16) * mm, v(301.01, -106.89) * mm]});
            skFitSpline(sketch, "E249", {"points": [v(301.01, -106.89) * mm, v(330.9, -109.06) * mm, v(360.83, -110.54) * mm, v(390.75, -112.08) * mm]});
            skFitSpline(sketch, "E250", {"points": [v(390.75, -112.08) * mm, v(414.91, -113.33) * mm, v(438.01, -118) * mm, v(456.04, -135.41) * mm]});
            skFitSpline(sketch, "E251", {"points": [v(456.04, -135.41) * mm, v(465.81, -144.85) * mm, v(474.08, -155.88) * mm, v(482.77, -166.4) * mm]});
            skFitSpline(sketch, "E252", {"points": [v(482.77, -166.4) * mm, v(502.2, -189.88) * mm, v(526.57, -206.58) * mm, v(554.27, -218.66) * mm]});
            skFitSpline(sketch, "E253", {"points": [v(554.27, -218.66) * mm, v(562.35, -222.18) * mm, v(567.4, -227.84) * mm, v(568.29, -236.5) * mm]});
            skFitSpline(sketch, "E254", {"points": [v(568.29, -236.5) * mm, v(569.22, -245.62) * mm, v(565.96, -253.24) * mm, v(558.03, -258.34) * mm]});
            skFitSpline(sketch, "E255", {"points": [v(558.03, -258.34) * mm, v(547.88, -264.86) * mm, v(536.6, -264.7) * mm, v(525.17, -263.7) * mm]});
            skFitSpline(sketch, "E256", {"points": [v(525.17, -263.7) * mm, v(505.67, -261.97) * mm, v(489.19, -253.05) * mm, v(474.22, -241.33) * mm]});
            skFitSpline(sketch, "E257", {"points": [v(474.22, -241.33) * mm, v(457.18, -227.98) * mm, v(440.32, -214.34) * mm, v(424.13, -199.97) * mm, v(397.92, -176.73) * mm, v(366.84, -166.61) * mm, v(332.73, -162.97) * mm]});
            skFitSpline(sketch, "E258", {"points": [v(332.73, -162.97) * mm, v(292.34, -158.65) * mm, v(251.84, -160.68) * mm, v(211.39, -159.98) * mm, v(188.93, -159.6) * mm, v(166.98, -156.35) * mm, v(145.8, -148.51) * mm]});
            skFitSpline(sketch, "E259", {"points": [v(145.8, -148.51) * mm, v(106.86, -134.1) * mm, v(77.34, -108.06) * mm, v(54.38, -74.08) * mm]});
            skFitSpline(sketch, "E260", {"points": [v(54.38, -74.08) * mm, v(48.52, -65.4) * mm, v(43.32, -56.26) * mm, v(38.12, -47.16) * mm]});
            skFitSpline(sketch, "E261", {"points": [v(38.12, -47.16) * mm, v(21.88, -18.74) * mm, v(0.84, 5.52) * mm, v(-24.95, 25.61) * mm]});
            skFitSpline(sketch, "E262", {"points": [v(-24.95, 25.61) * mm, v(-30.05, 29.58) * mm, v(-35.82, 32.68) * mm, v(-41.31, 36.14) * mm]});
            skFitSpline(sketch, "E263", {"points": [v(-41.31, 36.14) * mm, v(-42.38, 36.8) * mm, v(-43.6, 37.24) * mm, v(-45.49, 38.13) * mm]});
            skFitSpline(sketch, "E264", {"points": [v(-45.49, 38.13) * mm, v(-39.2, 31.2) * mm, v(-32.98, 25.38) * mm, v(-28.04, 18.62) * mm]});
            skFitSpline(sketch, "E265", {"points": [v(-28.04, 18.62) * mm, v(-24, 13.1) * mm, v(-21.3, 6.56) * mm, v(-18.37, 0.3) * mm]});
            skFitSpline(sketch, "E266", {"points": [v(-18.37, 0.3) * mm, v(-17.17, -2.25) * mm, v(-18.12, -4.01) * mm, v(-21.57, -4.03) * mm]});
            skFitSpline(sketch, "E267", {"points": [v(-21.57, -4.03) * mm, v(-64.04, -4.2) * mm, v(-106.52, -5.04) * mm, v(-148.99, -4.55) * mm]});
            skFitSpline(sketch, "E268", {"points": [v(-148.99, -4.55) * mm, v(-198.83, -3.97) * mm, v(-246, 8.98) * mm, v(-291.36, 29.07) * mm]});
            skFitSpline(sketch, "E269", {"points": [v(-291.36, 29.07) * mm, v(-293.77, 30.14) * mm, v(-296.02, 30.78) * mm, v(-295.79, 34.56) * mm]});
            skFitSpline(sketch, "E270", {"points": [v(-295.79, 34.56) * mm, v(-294.72, 52.24) * mm, v(-297.01, 69.45) * mm, v(-304.63, 86.6) * mm]});
            skFitSpline(sketch, "E271", {"points": [v(-304.63, 86.6) * mm, v(-246.06, 68.65) * mm, v(-187.48, 55.68) * mm, v(-126.4, 60.84) * mm]});
            skFitSpline(sketch, "E272", {"points": [v(-126.4, 60.84) * mm, v(-200.85, 69.54) * mm, v(-272.36, 86.56) * mm, v(-333.75, 131.9) * mm]});
            skFitSpline(sketch, "E273", {"points": [v(-333.75, 131.9) * mm, v(-331.23, 118.27) * mm, v(-328.31, 104.45) * mm, v(-326.2, 90.51) * mm, v(-324.04, 76.32) * mm, v(-323.43, 62.03) * mm, v(-326.14, 47.76) * mm]});
            skFitSpline(sketch, "E274", {"points": [v(-326.14, 47.76) * mm, v(-328.89, 33.33) * mm, v(-337.15, 23.03) * mm, v(-349.62, 15.86) * mm]});
            skFitSpline(sketch, "E275", {"points": [v(-349.62, 15.86) * mm, v(-366.14, 6.38) * mm, v(-384.25, 4.5) * mm, v(-402.78, 5.48) * mm]});
            skFitSpline(sketch, "E276", {"points": [v(-402.78, 5.48) * mm, v(-425.73, 6.7) * mm, v(-447.77, 12.25) * mm, v(-469.4, 19.81) * mm, v(-494.46, 28.56) * mm, v(-519.99, 35.41) * mm, v(-546.67, 36.96) * mm]});
            skFitSpline(sketch, "E277", {"points": [v(-546.67, 36.96) * mm, v(-555.94, 37.5) * mm, v(-565.13, 36.6) * mm, v(-573.53, 32.65) * mm]});
            skFitSpline(sketch, "E278", {"points": [v(-573.53, 32.65) * mm, v(-577.84, 30.6) * mm, v(-582.12, 27.36) * mm, v(-584.94, 23.57) * mm]});
            skFitSpline(sketch, "E279", {"points": [v(-584.94, 23.57) * mm, v(-588.8, 18.4) * mm, v(-586.65, 11.94) * mm, v(-580.62, 9.53) * mm]});
            skFitSpline(sketch, "E280", {"points": [v(-580.62, 9.53) * mm, v(-574.36, 7.02) * mm, v(-573.4, 2.92) * mm, v(-577.78, -1.97) * mm]});
            skFitSpline(sketch, "E281", {"points": [v(-577.78, -1.97) * mm, v(-582.43, -7.16) * mm, v(-586.93, -12.62) * mm, v(-592.29, -17) * mm]});
            skFitSpline(sketch, "E282", {"points": [v(-592.29, -17) * mm, v(-603.33, -26.04) * mm, v(-620.04, -21.97) * mm, v(-626.76, -9.2) * mm]});
            skFitSpline(sketch, "E283", {"points": [v(-626.76, -9.2) * mm, v(-630.67, -1.78) * mm, v(-630.26, 5.84) * mm, v(-628.07, 13.61) * mm, v(-621.63, 36.42) * mm, v(-606.2, 51.15) * mm, v(-585.44, 61.1) * mm]});
            skFitSpline(sketch, "E284", {"points": [v(-585.44, 61.1) * mm, v(-563.1, 71.8) * mm, v(-539.3, 75.8) * mm, v(-514.77, 76.62) * mm]});
            skFitSpline(sketch, "E285", {"points": [v(-514.77, 76.62) * mm, v(-480.02, 77.77) * mm, v(-445.56, 74.95) * mm, v(-411.3, 69.32) * mm]});
            skFitSpline(sketch, "E286", {"points": [v(-411.3, 69.32) * mm, v(-409.84, 69.08) * mm, v(-408.36, 69) * mm, v(-406.69, 69.64) * mm]});
            skFitSpline(sketch, "E287", {"points": [v(-406.69, 69.64) * mm, v(-411.44, 71.05) * mm, v(-416.29, 72.21) * mm, v(-420.94, 73.91) * mm]});
            skFitSpline(sketch, "E288", {"points": [v(-420.94, 73.91) * mm, v(-432.33, 78.07) * mm, v(-443.8, 82.1) * mm, v(-454.93, 86.86) * mm]});
            skFitSpline(sketch, "E289", {"points": [v(-454.93, 86.86) * mm, v(-476.6, 96.14) * mm, v(-489.62, 113.74) * mm, v(-498.98, 134.48) * mm]});
            skFitSpline(sketch, "E290", {"points": [v(-498.98, 134.48) * mm, v(-505, 147.8) * mm, v(-510.62, 161.3) * mm, v(-516.32, 174.5) * mm]});
            skFitSpline(sketch, "E291", {"points": [v(-516.32, 174.5) * mm, v(-522.03, 165.88) * mm, v(-520.18, 143.25) * mm, v(-510.55, 109.45) * mm]});
            skFitSpline(sketch, "E292", {"points": [v(-510.55, 109.45) * mm, v(-511.54, 110.36) * mm, v(-512.12, 110.75) * mm, v(-512.51, 111.27) * mm]});
            skFitSpline(sketch, "E293", {"points": [v(-512.51, 111.27) * mm, v(-540.91, 149.17) * mm, v(-579.72, 170.03) * mm, v(-625.2, 179.62) * mm]});
            skFitSpline(sketch, "E294", {"points": [v(-625.2, 179.62) * mm, v(-635.43, 181.77) * mm, v(-642.15, 187.24) * mm, v(-646.79, 196.27) * mm]});
            skFitSpline(sketch, "E295", {"points": [v(-646.79, 196.27) * mm, v(-652.87, 208.1) * mm, v(-660.61, 218.72) * mm, v(-671.96, 226.1) * mm, v(-675.78, 228.57) * mm, v(-680.15, 230.19) * mm, v(-684.69, 231.76) * mm]});
            skFitSpline(sketch, "E296", {"points": [v(-684.69, 231.76) * mm, v(-679.77, 222.65) * mm, v(-677.19, 213.22) * mm, v(-676.62, 203.18) * mm, v(-675.81, 188.76) * mm, v(-681.1, 176.86) * mm, v(-692.37, 168.25) * mm]});
            skFitSpline(sketch, "E297", {"points": [v(-692.37, 168.25) * mm, v(-699.04, 163.16) * mm, v(-706.62, 158.99) * mm, v(-714.34, 155.66) * mm]});
            skFitSpline(sketch, "E298", {"points": [v(-714.34, 155.66) * mm, v(-719.7, 153.34) * mm, v(-724.07, 150.3) * mm, v(-728.24, 146.42) * mm]});
            skFitSpline(sketch, "E299", {"points": [v(-728.24, 146.42) * mm, v(-735.2, 139.97) * mm, v(-742.14, 133.46) * mm, v(-749.64, 127.67) * mm]});
            skFitSpline(sketch, "E300", {"points": [v(-749.64, 127.67) * mm, v(-753.74, 124.51) * mm, v(-758.82, 122.44) * mm, v(-763.7, 120.53) * mm]});
            skFitSpline(sketch, "E301", {"points": [v(-763.7, 120.53) * mm, v(-767.91, 118.89) * mm, v(-771.88, 120.55) * mm, v(-775.28, 123.38) * mm]});
            skFitSpline(sketch, "E302", {"points": [v(-775.28, 123.38) * mm, v(-780, 127.33) * mm, v(-779.63, 129.63) * mm, v(-774.9, 133.58) * mm]});
            skFitSpline(sketch, "E303", {"points": [v(-774.9, 133.58) * mm, v(-764.66, 142.09) * mm, v(-754.1, 150.32) * mm, v(-744.8, 159.78) * mm]});
            skFitSpline(sketch, "E304", {"points": [v(-744.8, 159.78) * mm, v(-737.63, 167.08) * mm, v(-732.87, 174.42) * mm, v(-731.13, 182.91) * mm]});
            skFitSpline(sketch, "E305", {"points": [v(-731.13, 182.91) * mm, v(-729.4, 191.4) * mm, v(-730.7, 201.06) * mm, v(-735.67, 212.97) * mm, v(-741.37, 226.63) * mm, v(-755.23, 233.88) * mm, v(-769.84, 231.73) * mm]});
            skFitSpline(sketch, "E306", {"points": [v(-769.84, 231.73) * mm, v(-776.73, 230.72) * mm, v(-782.53, 227.39) * mm, v(-786.49, 221.65) * mm]});
            skFitSpline(sketch, "E307", {"points": [v(-786.49, 221.65) * mm, v(-792.25, 213.3) * mm, v(-797.58, 204.65) * mm, v(-803.19, 196.19) * mm]});
            skFitSpline(sketch, "E308", {"points": [v(-803.19, 196.19) * mm, v(-805.2, 193.14) * mm, v(-807.23, 190.05) * mm, v(-809.67, 187.35) * mm]});
            skFitSpline(sketch, "E309", {"points": [v(-809.67, 187.35) * mm, v(-816.17, 180.13) * mm, v(-824.16, 178.31) * mm, v(-832.66, 182.96) * mm]});
            skFitSpline(sketch, "E310", {"points": [v(-832.66, 182.96) * mm, v(-837.2, 185.45) * mm, v(-841.3, 189.17) * mm, v(-844.76, 193.08) * mm]});
            skFitSpline(sketch, "E311", {"points": [v(-844.76, 193.08) * mm, v(-848.93, 197.8) * mm, v(-848.62, 203.64) * mm, v(-845.8, 209.04) * mm, v(-837.04, 225.9) * mm, v(-823.25, 235.8) * mm, v(-804.27, 238.05) * mm, v(-798.82, 238.7) * mm, v(-793.27, 238.6) * mm, v(-787.84, 239.36) * mm]});
            skFitSpline(sketch, "E312", {"points": [v(-787.84, 239.36) * mm, v(-769.7, 241.9) * mm, v(-756.62, 252.41) * mm, v(-745.32, 266.64) * mm]});
            skFitSpline(sketch, "E313", {"points": [v(-745.32, 266.64) * mm, v(-752.1, 270.34) * mm, v(-759.1, 270) * mm, v(-765.96, 270.24) * mm, v(-768.62, 270.34) * mm, v(-771.28, 269.95) * mm, v(-773.94, 269.87) * mm, v(-786.66, 269.5) * mm, v(-795.12, 263) * mm, v(-800.28, 251.7) * mm]});
            skFitSpline(sketch, "E314", {"points": [v(-800.28, 251.7) * mm, v(-802.58, 246.64) * mm, v(-806.91, 245.4) * mm, v(-812.2, 248.3) * mm, v(-816.63, 250.74) * mm, v(-818.24, 256.23) * mm, v(-814.85, 260.24) * mm]});
            skFitSpline(sketch, "E315", {"points": [v(-814.85, 260.24) * mm, v(-811.47, 264.25) * mm, v(-807.55, 268.1) * mm, v(-803.14, 270.88) * mm]});
            skFitSpline(sketch, "E316", {"points": [v(-803.14, 270.88) * mm, v(-787.93, 280.43) * mm, v(-770.64, 284.29) * mm, v(-753.35, 287.94) * mm, v(-716.43, 295.75) * mm, v(-679.25, 295.26) * mm, v(-641.98, 291.14) * mm, v(-640.32, 290.96) * mm, v(-638.75, 289.88) * mm, v(-637.14, 289.22) * mm]});
            skFitSpline(sketch, "E317", {"points": [v(-637.14, 289.22) * mm, v(-637.93, 287.5) * mm, v(-638.31, 285.4) * mm, v(-639.55, 284.15) * mm, v(-656.61, 266.8) * mm, v(-677.4, 260.88) * mm, v(-701.17, 264.36) * mm, v(-703.46, 264.7) * mm, v(-705.72, 265.18) * mm, v(-708.42, 265.67) * mm]});
            skFitSpline(sketch, "E318", {"points": [v(-708.42, 265.67) * mm, v(-708.53, 260.53) * mm, v(-705.38, 257.14) * mm, v(-701.81, 255.38) * mm]});
            skFitSpline(sketch, "E319", {"points": [v(-701.81, 255.38) * mm, v(-693.22, 251.16) * mm, v(-684.48, 246.6) * mm, v(-675.27, 244.44) * mm]});
            skFitSpline(sketch, "E320", {"points": [v(-675.27, 244.44) * mm, v(-660.01, 240.87) * mm, v(-645.8, 235.12) * mm, v(-632.05, 227.94) * mm]});
            skFitSpline(sketch, "E321", {"points": [v(-632.05, 227.94) * mm, v(-611.47, 217.2) * mm, v(-592.36, 204.16) * mm, v(-574.04, 189.95) * mm]});
            skFitSpline(sketch, "E322", {"points": [v(-574.04, 189.95) * mm, v(-572.2, 188.53) * mm, v(-570.35, 187.13) * mm, v(-568.48, 185.7) * mm]});
            skFitSpline(sketch, "E323", {"points": [v(-568.48, 185.7) * mm, v(-568.27, 186.12) * mm, v(-567.98, 186.48) * mm, v(-568.06, 186.6) * mm]});
            skFitSpline(sketch, "E324", {"points": [v(-568.06, 186.6) * mm, v(-586.24, 215.93) * mm, v(-609.02, 240.28) * mm, v(-641.26, 254.42) * mm]});
            skFitSpline(sketch, "E325", {"points": [v(-641.26, 254.42) * mm, v(-642.94, 255.15) * mm, v(-644.78, 255.57) * mm, v(-646.34, 256.47) * mm]});
            skFitSpline(sketch, "E326", {"points": [v(-646.34, 256.47) * mm, v(-647.94, 257.4) * mm, v(-650.52, 258.8) * mm, v(-650.48, 259.9) * mm, v(-650.41, 261.65) * mm, v(-648.9, 264.07) * mm, v(-647.31, 264.89) * mm]});
            skFitSpline(sketch, "E327", {"points": [v(-647.31, 264.89) * mm, v(-637.75, 269.81) * mm, v(-628.32, 275.28) * mm, v(-618.23, 278.84) * mm]});
            skFitSpline(sketch, "E328", {"points": [v(-618.23, 278.84) * mm, v(-601.4, 284.77) * mm, v(-583.8, 284.01) * mm, v(-566.3, 281.85) * mm]});
            skFitSpline(sketch, "E329", {"points": [v(-566.3, 281.85) * mm, v(-522.8, 276.49) * mm, v(-480.6, 266.13) * mm, v(-440.4, 248.3) * mm, v(-409.85, 234.75) * mm, v(-381.84, 217.37) * mm, v(-358.18, 193.48) * mm]});
            skFitSpline(sketch, "E330", {"points": [v(-358.18, 193.48) * mm, v(-357.65, 192.95) * mm, v(-356.98, 192.55) * mm, v(-356.38, 192.09) * mm]});
            skFitSpline(sketch, "E331", {"points": [v(-356.38, 192.09) * mm, v(-355.88, 192.37) * mm, v(-355.38, 192.66) * mm, v(-354.88, 192.94) * mm]});
            skFitSpline(sketch, "E332", {"points": [v(-354.88, 192.94) * mm, v(-359.86, 203.36) * mm, v(-364.86, 213.77) * mm, v(-369.8, 224.2) * mm]});
            skFitSpline(sketch, "E333", {"points": [v(-369.8, 224.2) * mm, v(-370.6, 225.9) * mm, v(-371.1, 227.76) * mm, v(-371.73, 229.54) * mm]});
            skFitSpline(sketch, "E334", {"points": [v(-371.73, 229.54) * mm, v(-369.63, 230.22) * mm, v(-367.4, 231.74) * mm, v(-365.44, 231.44) * mm, v(-356.24, 230.07) * mm, v(-347, 228.63) * mm, v(-337.98, 226.42) * mm]});
            skFitSpline(sketch, "E335", {"points": [v(-337.98, 226.42) * mm, v(-286.2, 213.74) * mm, v(-236, 196.03) * mm, v(-185.76, 178.4) * mm]});
            skFitSpline(sketch, "E336", {"points": [v(-185.76, 178.4) * mm, v(-45.9, 129.3) * mm, v(90.23, 71.14) * mm, v(224.46, 8.53) * mm]});
            skFitSpline(sketch, "E337", {"points": [v(224.46, 8.53) * mm, v(269.82, -12.63) * mm, v(313.78, -36.77) * mm, v(358.44, -59.44) * mm]});
            skFitSpline(sketch, "E338", {"points": [v(358.44, -59.44) * mm, v(381, -70.88) * mm, v(403.96, -81.55) * mm, v(426.21, -93.53) * mm]});
            skFitSpline(sketch, "E339", {"points": [v(426.21, -93.53) * mm, v(448.48, -105.52) * mm, v(469.83, -119.2) * mm, v(492.05, -131.25) * mm]});
            skFitSpline(sketch, "E340", {"points": [v(492.05, -131.25) * mm, v(517.63, -145.14) * mm, v(543.25, -159.1) * mm, v(569.72, -171.12) * mm]});
            skFitSpline(sketch, "E341", {"points": [v(569.72, -171.12) * mm, v(595.41, -182.77) * mm, v(623, -186.7) * mm, v(651.26, -182.98) * mm]});
            skFitSpline(sketch, "E342", {"points": [v(651.26, -182.98) * mm, v(656.3, -182.31) * mm, v(661.24, -180.56) * mm, v(666.1, -178.92) * mm]});
            skFitSpline(sketch, "E343", {"points": [v(666.1, -178.92) * mm, v(674.75, -176) * mm, v(683.27, -172.68) * mm, v(691.93, -169.77) * mm]});
            skFitSpline(sketch, "E344", {"points": [v(691.93, -169.77) * mm, v(694.24, -168.99) * mm, v(696.84, -168.86) * mm, v(699.32, -168.84) * mm]});
            skFitSpline(sketch, "E345", {"points": [v(699.32, -168.84) * mm, v(710.3, -168.73) * mm, v(717.26, -178.07) * mm, v(712.73, -188.08) * mm]});
            skFitSpline(sketch, "E346", {"points": [v(712.73, -188.08) * mm, v(710.23, -193.6) * mm, v(705.96, -198.87) * mm, v(701.25, -202.76) * mm]});
            skFitSpline(sketch, "E347", {"points": [v(701.25, -202.76) * mm, v(686.02, -215.35) * mm, v(668, -221.32) * mm, v(648.4, -222.68) * mm]});
            skFitSpline(sketch, "E348", {"points": [v(648.4, -222.68) * mm, v(630.55, -223.92) * mm, v(612.77, -223.66) * mm, v(595.19, -219.93) * mm]});
            skFitSpline(sketch, "E349", {"points": [v(595.19, -219.93) * mm, v(593.4, -219.55) * mm, v(591.38, -219.35) * mm, v(589.95, -218.37) * mm]});
            skFitSpline(sketch, "E350", {"points": [v(589.95, -218.37) * mm, v(576.2, -208.93) * mm, v(559.75, -206.41) * mm, v(544.57, -200.7) * mm]});
            skFitSpline(sketch, "E351", {"points": [v(544.57, -200.7) * mm, v(525.18, -193.38) * mm, v(509.75, -180.72) * mm, v(495.44, -166.35) * mm]});
            skFitSpline(sketch, "E352", {"points": [v(495.44, -166.35) * mm, v(484.74, -155.6) * mm, v(474.02, -144.87) * mm, v(463.7, -133.78) * mm]});
            skFitSpline(sketch, "E353", {"points": [v(463.7, -133.78) * mm, v(448.05, -116.97) * mm, v(428.63, -108.74) * mm, v(406.1, -106.03) * mm, v(377.19, -102.57) * mm, v(348.36, -98.3) * mm, v(319.5, -94.4) * mm]});
            skFitSpline(sketch, "E354", {"points": [v(319.5, -94.4) * mm, v(290.2, -90.44) * mm, v(267.87, -75.08) * mm, v(250.27, -52.02) * mm]});
            skFitSpline(sketch, "E355", {"points": [v(250.27, -52.02) * mm, v(246.44, -47) * mm, v(242.53, -41.98) * mm, v(239.13, -36.66) * mm]});
            skFitSpline(sketch, "E356", {"points": [v(239.13, -36.66) * mm, v(230.59, -23.28) * mm, v(219.16, -13.12) * mm, v(205.03, -5.67) * mm]});
            skFitSpline(sketch, "E357", {"points": [v(-696.95, 276.56) * mm, v(-683.3, 273.98) * mm, v(-670.07, 274.8) * mm, v(-656.2, 281.48) * mm]});
            skFitSpline(sketch, "E358", {"points": [v(-656.2, 281.48) * mm, v(-671.26, 284.36) * mm, v(-684.74, 285.87) * mm, v(-696.95, 276.56) * mm]});
            skFitSpline(sketch, "E359", {"points": [v(-794.98, 247.88) * mm, v(-792.41, 259.54) * mm, v(-782.46, 263.83) * mm, v(-768.94, 259.43) * mm]});
            skFitSpline(sketch, "E360", {"points": [v(-768.94, 259.43) * mm, v(-771.76, 251.81) * mm, v(-781.12, 247.6) * mm, v(-794.98, 247.88) * mm]});
            skFitSpline(sketch, "E361", {"points": [v(-696.95, 276.56) * mm, v(-684.74, 285.87) * mm, v(-671.26, 284.36) * mm, v(-656.2, 281.48) * mm]});
            skFitSpline(sketch, "E362", {"points": [v(-656.2, 281.48) * mm, v(-670.07, 274.8) * mm, v(-683.3, 273.98) * mm, v(-696.95, 276.56) * mm]});
            skSolve(sketch);
        }
        {
            var Q0;
            {var subQ2=sQuery(id+"F0.wireOp",EDGE,"E52");Q0=makeQuery(id+"F0.imprint","IMPRINT",FACE,{"disambiguationData":[TD([[makeQuery(id+"F0.imprint","IMPRINT",EDGE,{"derivedFrom":subQ2}),-1.0]])]});}
            extrude(context, id + "F1", {"entities" : qUnion([Q0]), "depth" : (7 / 0.05) * mm, "offsetDistance" : 25 * mm});
        }
        {
            var Q0;
            Q0=makeQuery(id+"F1.opExtrude","SWEPT_BODY",BODY,{"disambiguationData":[OSD([sQuery(id+"F0.wireOp",EDGE,"E52"),sQuery(id+"F0.wireOp",EDGE,"E70"),sQuery(id+"F0.wireOp",EDGE,"E71"),sQuery(id+"F0.wireOp",EDGE,"E72"),sQuery(id+"F0.wireOp",EDGE,"E73"),sQuery(id+"F0.wireOp",EDGE,"E74"),sQuery(id+"F0.wireOp",EDGE,"E75"),sQuery(id+"F0.wireOp",EDGE,"E76"),sQuery(id+"F0.wireOp",EDGE,"E77"),sQuery(id+"F0.wireOp",EDGE,"E78"),sQuery(id+"F0.wireOp",EDGE,"E79"),sQuery(id+"F0.wireOp",EDGE,"E80"),sQuery(id+"F0.wireOp",EDGE,"E81"),sQuery(id+"F0.wireOp",EDGE,"E82"),sQuery(id+"F0.wireOp",EDGE,"E83"),sQuery(id+"F0.wireOp",EDGE,"E84"),sQuery(id+"F0.wireOp",EDGE,"E85"),sQuery(id+"F0.wireOp",EDGE,"E86"),sQuery(id+"F0.wireOp",EDGE,"E87"),sQuery(id+"F0.wireOp",EDGE,"E88"),sQuery(id+"F0.wireOp",EDGE,"E89"),sQuery(id+"F0.wireOp",EDGE,"E90"),sQuery(id+"F0.wireOp",EDGE,"E91"),sQuery(id+"F0.wireOp",EDGE,"E92"),sQuery(id+"F0.wireOp",EDGE,"E93"),sQuery(id+"F0.wireOp",EDGE,"E94"),sQuery(id+"F0.wireOp",EDGE,"E95"),sQuery(id+"F0.wireOp",EDGE,"E96"),sQuery(id+"F0.wireOp",EDGE,"E97"),sQuery(id+"F0.wireOp",EDGE,"E98"),sQuery(id+"F0.wireOp",EDGE,"E99"),sQuery(id+"F0.wireOp",EDGE,"E100"),sQuery(id+"F0.wireOp",EDGE,"E101"),sQuery(id+"F0.wireOp",EDGE,"E102"),sQuery(id+"F0.wireOp",EDGE,"E103"),sQuery(id+"F0.wireOp",EDGE,"E104"),sQuery(id+"F0.wireOp",EDGE,"E105"),sQuery(id+"F0.wireOp",EDGE,"E106"),sQuery(id+"F0.wireOp",EDGE,"E107"),sQuery(id+"F0.wireOp",EDGE,"E108"),sQuery(id+"F0.wireOp",EDGE,"E109"),sQuery(id+"F0.wireOp",EDGE,"E110"),sQuery(id+"F0.wireOp",EDGE,"E111"),sQuery(id+"F0.wireOp",EDGE,"E112"),sQuery(id+"F0.wireOp",EDGE,"E113"),sQuery(id+"F0.wireOp",EDGE,"E114"),sQuery(id+"F0.wireOp",EDGE,"E115"),sQuery(id+"F0.wireOp",EDGE,"E116"),sQuery(id+"F0.wireOp",EDGE,"E117"),sQuery(id+"F0.wireOp",EDGE,"E118"),sQuery(id+"F0.wireOp",EDGE,"E119"),sQuery(id+"F0.wireOp",EDGE,"E120"),sQuery(id+"F0.wireOp",EDGE,"E121"),sQuery(id+"F0.wireOp",EDGE,"E122"),sQuery(id+"F0.wireOp",EDGE,"E123"),sQuery(id+"F0.wireOp",EDGE,"E124"),sQuery(id+"F0.wireOp",EDGE,"E125"),sQuery(id+"F0.wireOp",EDGE,"E126"),sQuery(id+"F0.wireOp",EDGE,"E127"),sQuery(id+"F0.wireOp",EDGE,"E128"),sQuery(id+"F0.wireOp",EDGE,"E129"),sQuery(id+"F0.wireOp",EDGE,"E130"),sQuery(id+"F0.wireOp",EDGE,"E131"),sQuery(id+"F0.wireOp",EDGE,"E132"),sQuery(id+"F0.wireOp",EDGE,"E246"),sQuery(id+"F0.wireOp",EDGE,"E247"),sQuery(id+"F0.wireOp",EDGE,"E248"),sQuery(id+"F0.wireOp",EDGE,"E249"),sQuery(id+"F0.wireOp",EDGE,"E250"),sQuery(id+"F0.wireOp",EDGE,"E251"),sQuery(id+"F0.wireOp",EDGE,"E252"),sQuery(id+"F0.wireOp",EDGE,"E253"),sQuery(id+"F0.wireOp",EDGE,"E254"),sQuery(id+"F0.wireOp",EDGE,"E255"),sQuery(id+"F0.wireOp",EDGE,"E256"),sQuery(id+"F0.wireOp",EDGE,"E257"),sQuery(id+"F0.wireOp",EDGE,"E258"),sQuery(id+"F0.wireOp",EDGE,"E259"),sQuery(id+"F0.wireOp",EDGE,"E260"),sQuery(id+"F0.wireOp",EDGE,"E261"),sQuery(id+"F0.wireOp",EDGE,"E262"),sQuery(id+"F0.wireOp",EDGE,"E263"),sQuery(id+"F0.wireOp",EDGE,"E264"),sQuery(id+"F0.wireOp",EDGE,"E265"),sQuery(id+"F0.wireOp",EDGE,"E266"),sQuery(id+"F0.wireOp",EDGE,"E267"),sQuery(id+"F0.wireOp",EDGE,"E268"),sQuery(id+"F0.wireOp",EDGE,"E269"),sQuery(id+"F0.wireOp",EDGE,"E270"),sQuery(id+"F0.wireOp",EDGE,"E271"),sQuery(id+"F0.wireOp",EDGE,"E272"),sQuery(id+"F0.wireOp",EDGE,"E273"),sQuery(id+"F0.wireOp",EDGE,"E274"),sQuery(id+"F0.wireOp",EDGE,"E275"),sQuery(id+"F0.wireOp",EDGE,"E276"),sQuery(id+"F0.wireOp",EDGE,"E277"),sQuery(id+"F0.wireOp",EDGE,"E278"),sQuery(id+"F0.wireOp",EDGE,"E279"),sQuery(id+"F0.wireOp",EDGE,"E280"),sQuery(id+"F0.wireOp",EDGE,"E281"),sQuery(id+"F0.wireOp",EDGE,"E282"),sQuery(id+"F0.wireOp",EDGE,"E283"),sQuery(id+"F0.wireOp",EDGE,"E284"),sQuery(id+"F0.wireOp",EDGE,"E285"),sQuery(id+"F0.wireOp",EDGE,"E286"),sQuery(id+"F0.wireOp",EDGE,"E287"),sQuery(id+"F0.wireOp",EDGE,"E288"),sQuery(id+"F0.wireOp",EDGE,"E289"),sQuery(id+"F0.wireOp",EDGE,"E290"),sQuery(id+"F0.wireOp",EDGE,"E291"),sQuery(id+"F0.wireOp",EDGE,"E292"),sQuery(id+"F0.wireOp",EDGE,"E293"),sQuery(id+"F0.wireOp",EDGE,"E294"),sQuery(id+"F0.wireOp",EDGE,"E295"),sQuery(id+"F0.wireOp",EDGE,"E296"),sQuery(id+"F0.wireOp",EDGE,"E297"),sQuery(id+"F0.wireOp",EDGE,"E298"),sQuery(id+"F0.wireOp",EDGE,"E299"),sQuery(id+"F0.wireOp",EDGE,"E300"),sQuery(id+"F0.wireOp",EDGE,"E301"),sQuery(id+"F0.wireOp",EDGE,"E302"),sQuery(id+"F0.wireOp",EDGE,"E303"),sQuery(id+"F0.wireOp",EDGE,"E304"),sQuery(id+"F0.wireOp",EDGE,"E305"),sQuery(id+"F0.wireOp",EDGE,"E306"),sQuery(id+"F0.wireOp",EDGE,"E307"),sQuery(id+"F0.wireOp",EDGE,"E308"),sQuery(id+"F0.wireOp",EDGE,"E309"),sQuery(id+"F0.wireOp",EDGE,"E310"),sQuery(id+"F0.wireOp",EDGE,"E311"),sQuery(id+"F0.wireOp",EDGE,"E312"),sQuery(id+"F0.wireOp",EDGE,"E313"),sQuery(id+"F0.wireOp",EDGE,"E314"),sQuery(id+"F0.wireOp",EDGE,"E315"),sQuery(id+"F0.wireOp",EDGE,"E316"),sQuery(id+"F0.wireOp",EDGE,"E317"),sQuery(id+"F0.wireOp",EDGE,"E318"),sQuery(id+"F0.wireOp",EDGE,"E319"),sQuery(id+"F0.wireOp",EDGE,"E320"),sQuery(id+"F0.wireOp",EDGE,"E321"),sQuery(id+"F0.wireOp",EDGE,"E322"),sQuery(id+"F0.wireOp",EDGE,"E323"),sQuery(id+"F0.wireOp",EDGE,"E324"),sQuery(id+"F0.wireOp",EDGE,"E325"),sQuery(id+"F0.wireOp",EDGE,"E326"),sQuery(id+"F0.wireOp",EDGE,"E327"),sQuery(id+"F0.wireOp",EDGE,"E328"),sQuery(id+"F0.wireOp",EDGE,"E329"),sQuery(id+"F0.wireOp",EDGE,"E330"),sQuery(id+"F0.wireOp",EDGE,"E331"),sQuery(id+"F0.wireOp",EDGE,"E332"),sQuery(id+"F0.wireOp",EDGE,"E333"),sQuery(id+"F0.wireOp",EDGE,"E334"),sQuery(id+"F0.wireOp",EDGE,"E335"),sQuery(id+"F0.wireOp",EDGE,"E336"),sQuery(id+"F0.wireOp",EDGE,"E337"),sQuery(id+"F0.wireOp",EDGE,"E338"),sQuery(id+"F0.wireOp",EDGE,"E339"),sQuery(id+"F0.wireOp",EDGE,"E340"),sQuery(id+"F0.wireOp",EDGE,"E341"),sQuery(id+"F0.wireOp",EDGE,"E342"),sQuery(id+"F0.wireOp",EDGE,"E343"),sQuery(id+"F0.wireOp",EDGE,"E344"),sQuery(id+"F0.wireOp",EDGE,"E345"),sQuery(id+"F0.wireOp",EDGE,"E346"),sQuery(id+"F0.wireOp",EDGE,"E347"),sQuery(id+"F0.wireOp",EDGE,"E348"),sQuery(id+"F0.wireOp",EDGE,"E349"),sQuery(id+"F0.wireOp",EDGE,"E350"),sQuery(id+"F0.wireOp",EDGE,"E351"),sQuery(id+"F0.wireOp",EDGE,"E352"),sQuery(id+"F0.wireOp",EDGE,"E353"),sQuery(id+"F0.wireOp",EDGE,"E354"),sQuery(id+"F0.wireOp",EDGE,"E355"),sQuery(id+"F0.wireOp",EDGE,"E356"),sQuery(id+"F0.wireOp",EDGE,"E359"),sQuery(id+"F0.wireOp",EDGE,"E360")])]});
            var Q1;
            Q1=qCreatedBy(makeId("Origin.pointOp"),VERTEX);
            transform(context, id + "F2", {"entities" : qUnion([Q0]), "transformType" : TransformType.SCALE_UNIFORMLY, "scale" : .5, "scalePoint" : qUnion([Q1]), "makeCopy" : false});
        }
    });
